# Revit family: Сенсорная кнопка AGRG AXI_тип модель
name_source: partatom
category: Охранная сигнализация
units: mm (PartAtom-declared; Revit-internal decimal feet)

## family parameters
Всегда вертикально = Да
На основе рабочей плоскости = Нет
Общий = Нет
При загрузке вырезать с полостями = Нет
Размер круглого соединителя = Использовать диаметр
Сохранять ориентацию аннотаций = Нет
Тип детали = Нормальный
Точка расчета площади = Нет

## types (3) — shared parameters
ADSK_Верхний порог напряжения = 15 В
ADSK_Группирование = 1. Оборудование
ADSK_Единица измерения = шт.
ADSK_Завод-изготовитель = ООО «Агрегатор»
ADSK_Классификация нагрузок = Прочее
ADSK_Количество = 1
ADSK_Количество фаз = 1
ADSK_Коэффициент мощности = 1
ADSK_Марка = AGRG AXI
ADSK_Масса = 0.06
ADSK_Наименование краткое = Кнопка выход
ADSK_Нижний порог напряжения = 8 В
ADSK_Обозначение = SQ
ITV_SUB_УГО на структурной схеме = УГО_Кнопка выход
URL = https://skud.agrg.ru
Изображение типоразмера = SQ.png
Описание = ITV
zero-valued in all types: Стоимость

## per-type parameters (varying)
| type | ADSK_Код изделия | ADSK_Наименование | Материал |
| Сенсорная кнопка AGRG AXI «Арктический белый» | AXIBTNAW | Кнопка выхода для СКУД AGRG AXI "Арктический белый" | Пластмасса, непрозрачная, белая |
| Сенсорная кнопка AGRG AXI «Люксовый Мандарин» | AXIBTNLM | Кнопка выхода для СКУД AGRG AXI "Люксовый мандарин" | Пластмасса, непрозрачная, оранжевая |
| Сенсорная кнопка AGRG AXI «Имперский черный» | AXIBTNIBL | Кнопка выхода для СКУД AGRG AXI "Имперский черный" | Пластмасса, непрозрачная, черная |
